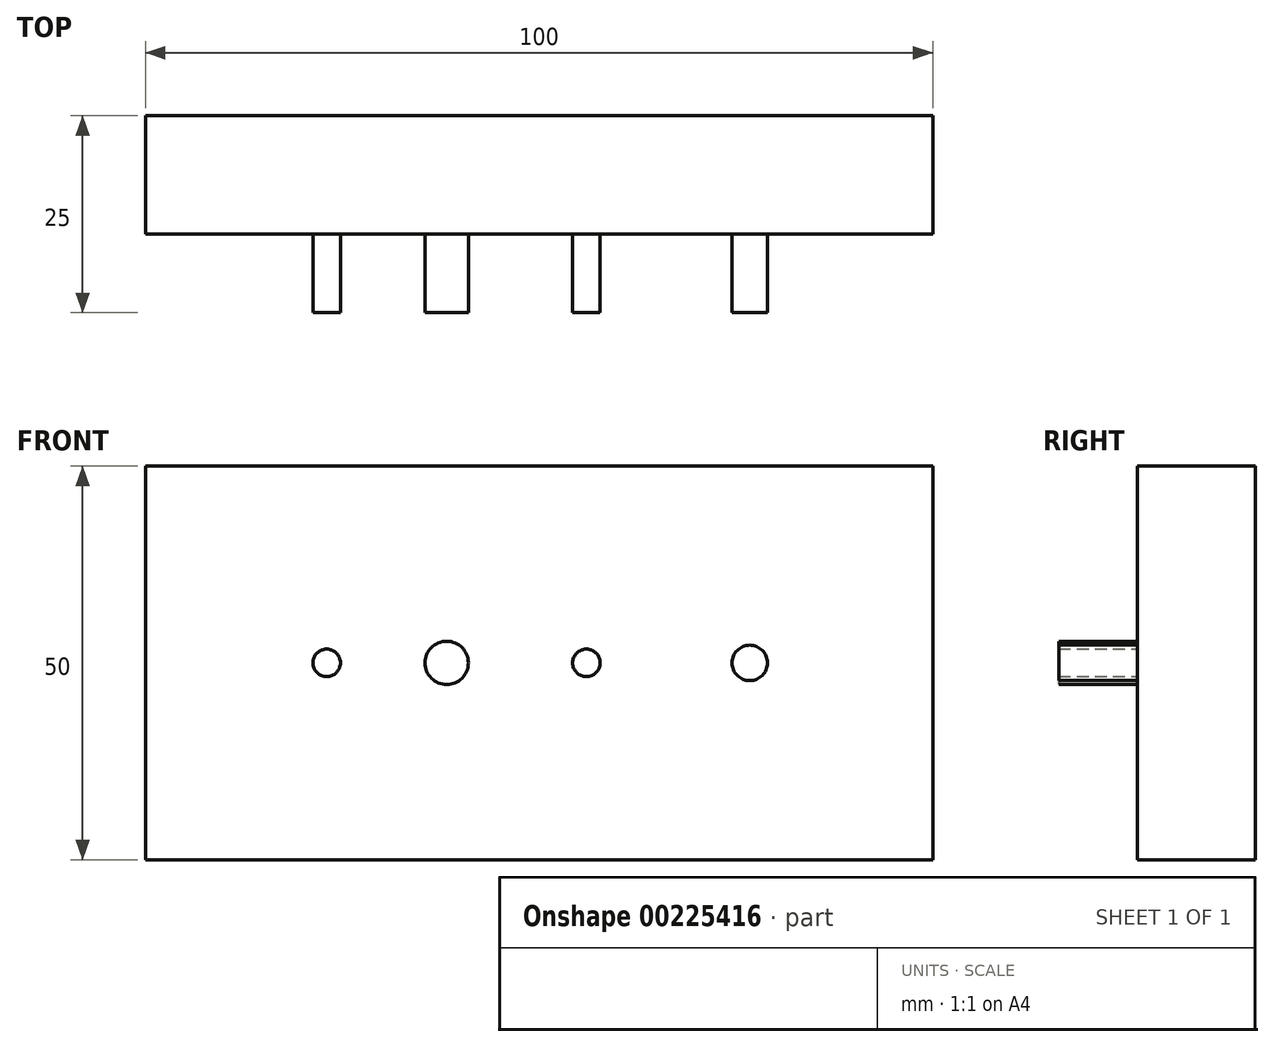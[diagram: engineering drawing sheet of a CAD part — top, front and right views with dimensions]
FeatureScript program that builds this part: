
annotation { "Feature Type Name" : "Feature", "Feature Type Description" : "" }
export const myFeature = defineFeature(function(context is Context, id is Id, definition is map)
    precondition{}
    {
        {
            var Q0;
            Q0=qCreatedBy(makeId("Front.planeOp"),FACE);
            var sketch = newSketch(context, id + "F0", { "sketchPlane" : qUnion([Q0])});
            skLineSegment(sketch, "E0.bottom", {"start": v(50, 25) * mm, "end": v(-50, 25) * mm});
            skLineSegment(sketch, "E0.top", {"start": v(50, -25) * mm, "end": v(-50, -25) * mm});
            skLineSegment(sketch, "E0.left", {"start": v(50, 25) * mm, "end": v(50, -25) * mm});
            skLineSegment(sketch, "E0.right", {"start": v(-50, 25) * mm, "end": v(-50, -25) * mm});
            skPoint(sketch, "E0.middle", {"position": v(0, 0) * mm});
            skSolve(sketch);
        }
        {
            var Q0;
            Q0=qSketchRegion(id+"F0",true);
            extrude(context, id + "F1", {"entities" : qUnion([Q0]), "depth" : 15 * mm});
        }
        {
            var Q0;
            Q0=makeQuery(id+"F1.opExtrude","CAP_FACE",FACE,{"disambiguationData":[OSD([sQuery(id+"F0.wireOp",EDGE,"E0.bottom"),sQuery(id+"F0.wireOp",EDGE,"E0.top"),sQuery(id+"F0.wireOp",EDGE,"E0.left"),sQuery(id+"F0.wireOp",EDGE,"E0.right")])],"isStart":false});
            var sketch = newSketch(context, id + "F2", { "sketchPlane" : qUnion([Q0])});
            skCircle(sketch, "E1", {"center": v(-27, 0) * mm, "radius": 1.75 * mm});
            skPoint(sketch, "E1.centerSnap0", {"position": v(-50, 0) * mm});
            skSolve(sketch);
        }
        {
            var Q0;
            Q0=makeQuery(id+"F2.imprint","IMPRINT",FACE,{"disambiguationData":[TD([[makeQuery(id+"F2.imprint","IMPRINT",EDGE,{"derivedFrom":sQuery(id+"F2.wireOp",EDGE,"E1")}),1.0]])]});
            extrude(context, id + "F3", {"entities" : qUnion([Q0]), "operationType" : NewBodyOperationType.ADD, "depth" : 10 * mm});
        }
        {
            var Q0;
            Q0=makeQuery(id+"F1.opExtrude","CAP_FACE",FACE,{"disambiguationData":[OSD([sQuery(id+"F0.wireOp",EDGE,"E0.bottom"),sQuery(id+"F0.wireOp",EDGE,"E0.top"),sQuery(id+"F0.wireOp",EDGE,"E0.left"),sQuery(id+"F0.wireOp",EDGE,"E0.right")])],"isStart":false});
            var sketch = newSketch(context, id + "F4", { "sketchPlane" : qUnion([Q0])});
            skCircle(sketch, "E2", {"center": v(-11.75, 0) * mm, "radius": 2.75 * mm});
            skSolve(sketch);
        }
        {
            var Q0;
            Q0=qSketchRegion(id+"F4",true);
            extrude(context, id + "F5", {"entities" : qUnion([Q0]), "operationType" : NewBodyOperationType.ADD, "depth" : 10 * mm});
        }
        {
            var Q0;
            Q0=makeQuery(id+"F1.opExtrude","CAP_FACE",FACE,{"disambiguationData":[OSD([sQuery(id+"F0.wireOp",EDGE,"E0.bottom"),sQuery(id+"F0.wireOp",EDGE,"E0.top"),sQuery(id+"F0.wireOp",EDGE,"E0.left"),sQuery(id+"F0.wireOp",EDGE,"E0.right")])],"isStart":false});
            var sketch = newSketch(context, id + "F6", { "sketchPlane" : qUnion([Q0])});
            skCircle(sketch, "E3", {"center": v(6, 0) * mm, "radius": 1.75 * mm});
            skSolve(sketch);
        }
        {
            var Q0;
            Q0=qSketchRegion(id+"F6",true);
            extrude(context, id + "F7", {"entities" : qUnion([Q0]), "operationType" : NewBodyOperationType.ADD, "depth" : 10 * mm});
        }
        {
            var Q0;
            Q0=makeQuery(id+"F1.opExtrude","CAP_FACE",FACE,{"disambiguationData":[OSD([sQuery(id+"F0.wireOp",EDGE,"E0.bottom"),sQuery(id+"F0.wireOp",EDGE,"E0.top"),sQuery(id+"F0.wireOp",EDGE,"E0.left"),sQuery(id+"F0.wireOp",EDGE,"E0.right")])],"isStart":false});
            var sketch = newSketch(context, id + "F8", { "sketchPlane" : qUnion([Q0])});
            skCircle(sketch, "E4", {"center": v(26.75, 0) * mm, "radius": 2.25 * mm});
            skSolve(sketch);
        }
        {
            var Q0;
            Q0=qSketchRegion(id+"F8",true);
            extrude(context, id + "F9", {"entities" : qUnion([Q0]), "operationType" : NewBodyOperationType.ADD, "depth" : 10 * mm});
        }
    });
